# Revit family: Dallmeier_Box_Cameras_en
name_source: partatom
category: Sicherheitsgeräte
units: mm (PartAtom-declared; Revit-internal decimal feet)

## family parameters
Basisbauteil = Fläche
Beim Laden mit Abzugskörper schneiden = Nein
Bemaßung runder Anschluss = Durchmesser verwenden
Beschriftungsausrichtung beibehalten = Nein
Gemeinsam genutzt = Nein
Raumberechnungspunkt = Nein
Teiletyp = Normal

## types (8) — shared parameters
4:3 Available = Ja
Hersteller = Dallmeier electronic GmbH
URL = https://www.dallmeier.com
Vorgabe-Ansicht = 122 cm
number of sensors = 1

## per-type parameters (varying)
| type | Long Horizontal FOV | Modell | Pixel Horizontal 16:9 | Pixel Horizontal 4:3 | Short Horizontal FOV | Show_BoxCase | Show_Nightline MDF | dimensions | operating temperature | power consumption | voltage supply | weight |
| DF Ultraline 5450HD-DN/IR 4-10mm | 105,00° | Dallmeier Box DF 5450 4-10mm | 3840 | 3840 | 42,00° | Ja | Nein | 99x88x231mm | -40°C to +50°C | 13 W | 12 V | 2,20 kg |
| DF Nightline 5250HD-DN/IR 4,5-10mm | 87,00° | Dallmeier Box DF 5250 4,5-10mm | 1920 | 1440 | 40,00° | Ja | Nein | 99x88x231mm | -40°C to +50°C | 13 W | 12 V | 2,20 kg |
| DF Primeline 5120HD-DN/IR 3-10mm | 111,00° | Dallmeier Box DF 5120 3-10mm | 1920 | 1440 | 31,90° | Ja | Nein | 99x88x231mm | -40°C to +50°C | 13 W | 12 V | 2,20 kg |
| DF Primeline 5140HD-DN/IR 3-10mm | 111,00° | Dallmeier Box DF 5140 3-10mm | 2592 | 2592 | 31,90° | Ja | Nein | 99x88x231mm | -40°C to +50°C | 13 W | 12 V | 2,20 kg |
| Nightline MDF5250HD-DN 4,5-10mm | 87,00° | Dallmeier Box DF 5140 3-10mm | 1920 | 1440 | 40,00° | Nein | Ja | 59x59x80mm | -20°C to +45°C | 8 W | 24 V | 0,20 kg |
| Nightline MDF5250HD-DN 12-40mm | 35,00° | Dallmeier Box DF 5140 3-10mm | 1920 | 1440 | 11,00° | Nein | Ja | 59x59x80mm | -20°C to +45°C | 8 W | 24 V | 0,20 kg |
| DF Primeline 5120HD-DN/IR 12-40mm | 23,80° | Dallmeier Box DF 5120 3-10mm | 1920 | 1440 | 8,30° | Ja | Nein | 99x88x231mm | -40°C to +50°C | 13 W | 12 V | 2,20 kg |
| DF Primeline 5140HD-DN/IR 12-40mm | 23,80° | Dallmeier Box DF 5140 3-10mm | 2592 | 2592 | 8,30° | Ja | Nein | 99x88x231mm | -40°C to +50°C | 13 W | 12 V | 2,20 kg |

## geometry (parser evidence)
native form markers: Sweep x23
no freeform markers — native parametric forms only
